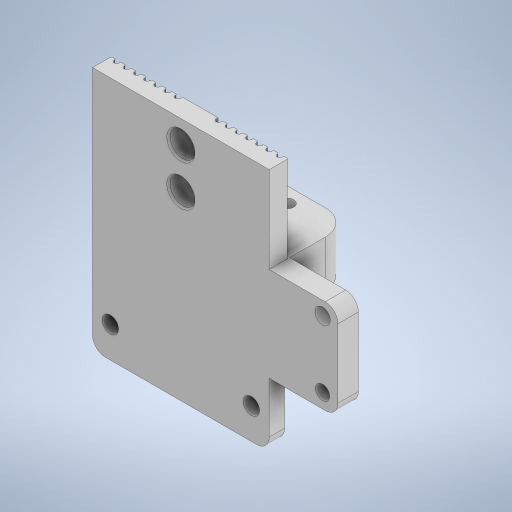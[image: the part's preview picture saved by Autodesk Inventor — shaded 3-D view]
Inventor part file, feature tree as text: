
AUTODESK INVENTOR PART (.ipt)
format: ipt  version: 2024.2 (Build 282272000, 272)  size: 580,608 bytes
history: native  units: in
note: dims shown in document units (in); Inventor stores cm internally (conversion verified against a paired STEP export)
features: other x4, direct_edit x3, extrude x2, sketch x2, fillet x1, projected_geometry x1, move_body x1
ambient origin geometry x8: Origin, YZ Plane, XZ Plane, XY Plane, X Axis, Y Axis, Z Axis, Center Point
bodies: Solid1 (feature_tree)
feature tree (14):
  direct_edit  "Direct Edit1"
  extrude  "Extrusion1"  TaperAngle=0.0deg  [1 undecoded]
  direct_edit  "Direct Edit2"
  direct_edit  "Direct Edit3"
  extrude  "Extrusion2"  Depth=0.0984in
  fillet  "Fillet1"  [1 undecoded]
  sketch  "Sketch1"  dims[d0=0.3937in d1=0.0in d2=0.0in d3=0.0in d4=-0.9843in]
  sketch  "Sketch2"  dims[d5=0.0in d6=0.0in d7=0.0984in]
  projected_geometry  "Projected Loop1"
  other  "carriage back plate"
  other  "Delete1"
  move_body  "Move1"
  other  "Delete2"
  other  "Delete3"
note: 2 required parameter values undecoded (feature->parameter linkage not recoverable at this tier; creation-order binding heuristic only, values carry confidence <= 0.55)
